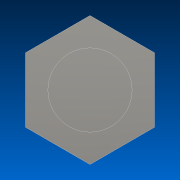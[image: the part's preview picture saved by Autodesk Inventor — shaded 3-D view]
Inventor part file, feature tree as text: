
AUTODESK INVENTOR PART (.ipt)
format: ipt  version: 2019 (Build 230136000, 136)  size: 107,520 bytes
history: native  units: mm
features: extrude x3, sketch x3, thread x2
ambient origin geometry x8: Origin, YZ Plane, XZ Plane, XY Plane, X Axis, Y Axis, Z Axis, Center Point
bodies: Body1 (feature_tree)
feature tree (8):
  extrude  "Extrusion3"  Depth=21.0mm TaperAngle=0.0deg
  extrude  "Extrusion4"  Depth=6.0mm TaperAngle=0.0deg
  thread  "Thread2"  [1 undecoded]
  extrude  "Extrusion5"  Depth=5.0mm TaperAngle=0.0deg
  thread  "Thread3"  [1 undecoded]
  sketch  "Sketch6"  dims[d15=4.6mm d16=21.0mm d17=0.0mm]
  sketch  "Sketch7"  dims[d18=3.0mm d19=6.0mm d20=0.0mm d21=10.0mm d22=0.0mm]
  sketch  "Sketch8"  dims[d23=3.0mm d24=5.0mm d25=0.0mm d26=10.0mm d27=0.0mm]
note: 2 required parameter values undecoded (feature->parameter linkage not recoverable at this tier; creation-order binding heuristic only, values carry confidence <= 0.55)
